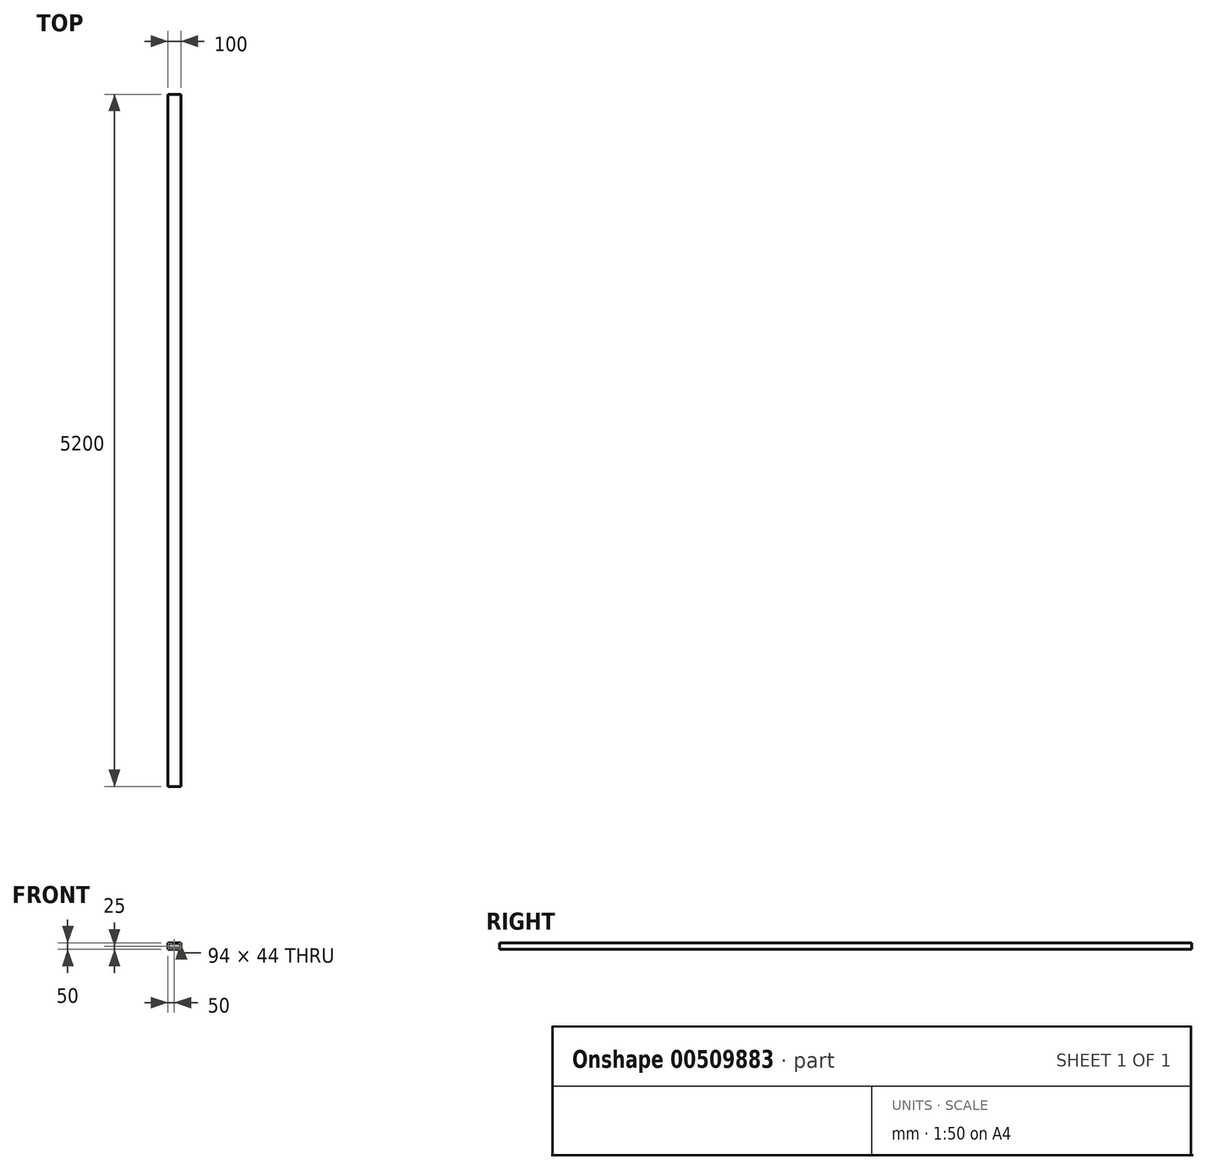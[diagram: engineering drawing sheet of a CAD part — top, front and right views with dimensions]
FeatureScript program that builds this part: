
annotation { "Feature Type Name" : "Feature", "Feature Type Description" : "" }
export const myFeature = defineFeature(function(context is Context, id is Id, definition is map)
    precondition{}
    {
        {
            var Q0;
            Q0=qCreatedBy(makeId("Front.planeOp"),FACE);
            var sketch = newSketch(context, id + "F0", { "sketchPlane" : qUnion([Q0])});
            skLineSegment(sketch, "E0.bottom", {"start": v(50, -25) * mm, "end": v(-50, -25) * mm});
            skLineSegment(sketch, "E0.top", {"start": v(50, 25) * mm, "end": v(-50, 25) * mm});
            skLineSegment(sketch, "E0.left", {"start": v(50, -25) * mm, "end": v(50, 25) * mm});
            skLineSegment(sketch, "E0.right", {"start": v(-50, -25) * mm, "end": v(-50, 25) * mm});
            skPoint(sketch, "E0.middle", {"position": v(0, 0) * mm});
            skLineSegment(sketch, "E1.bottom", {"start": v(47, -22) * mm, "end": v(-47, -22) * mm});
            skLineSegment(sketch, "E1.top", {"start": v(47, 22) * mm, "end": v(-47, 22) * mm});
            skLineSegment(sketch, "E1.left", {"start": v(47, -22) * mm, "end": v(47, 22) * mm});
            skLineSegment(sketch, "E1.right", {"start": v(-47, -22) * mm, "end": v(-47, 22) * mm});
            skSolve(sketch);
        }
        {
            var Q0;
            Q0=makeQuery(id+"F0.imprint","IMPRINT",FACE,{"disambiguationData":[TD([[makeQuery(id+"F0.imprint","IMPRINT",EDGE,{"derivedFrom":sQuery(id+"F0.wireOp",EDGE,"E0.bottom")}),-1.0]])]});
            extrude(context, id + "F1", {"entities" : qUnion([Q0]), "depth" : 5200 * mm, "offsetDistance" : 25 * mm});
        }
    });
